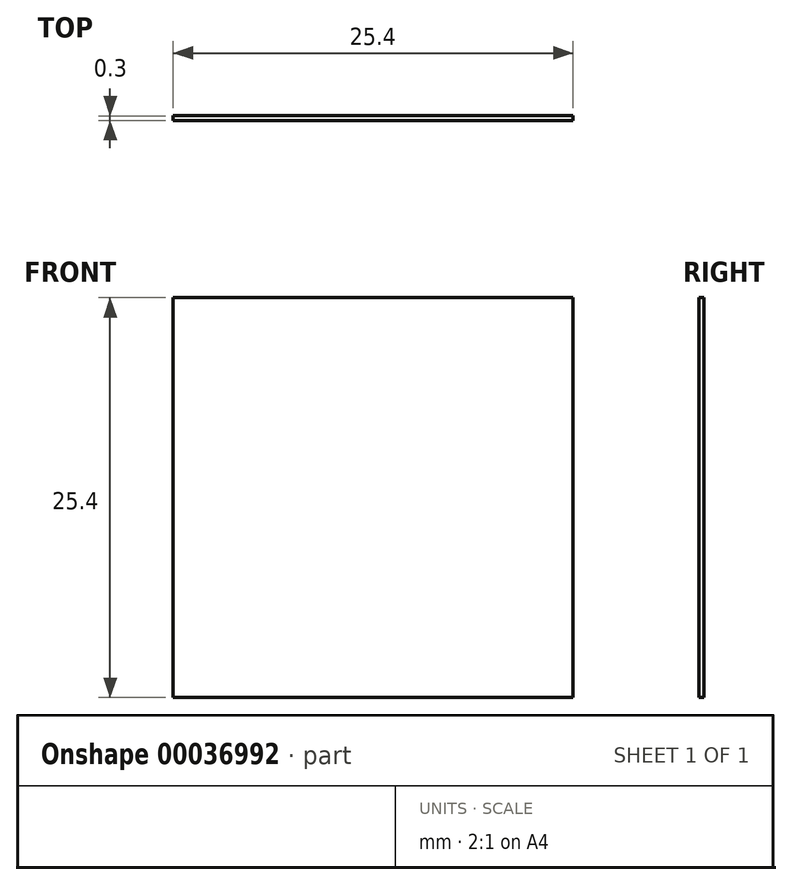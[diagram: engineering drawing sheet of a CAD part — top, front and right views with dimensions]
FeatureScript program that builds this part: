
annotation { "Feature Type Name" : "Feature", "Feature Type Description" : "" }
export const myFeature = defineFeature(function(context is Context, id is Id, definition is map)
    precondition{}
    {
        {
            var Q0;
            Q0=qCreatedBy(makeId("Top.planeOp"),FACE);
            var sketch = newSketch(context, id + "F0", { "sketchPlane" : qUnion([Q0])});
            skLineSegment(sketch, "E0.bottom", {"start": v(0, 0) * mm, "end": v(25.4, 0) * mm});
            skLineSegment(sketch, "E0.top", {"start": v(0, 0.3) * mm, "end": v(25.4, 0.3) * mm});
            skLineSegment(sketch, "E0.left", {"start": v(0, 0) * mm, "end": v(0, 0.3) * mm});
            skLineSegment(sketch, "E0.right", {"start": v(25.4, 0) * mm, "end": v(25.4, 0.3) * mm});
            skSolve(sketch);
        }
        {
            var Q0;
            Q0 = qSketchRegion(id + "F0", true);
            extrude(context, id + "F1", {"entities" : qUnion([Q0]), "depth" : 25.4 * mm});
        }
    });
